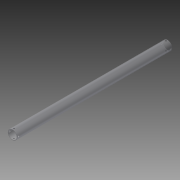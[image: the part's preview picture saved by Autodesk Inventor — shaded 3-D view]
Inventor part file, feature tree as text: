
AUTODESK INVENTOR PART (.ipt)
format: ipt  version: 2014 (Build 180170000, 170)  size: 145,408 bytes
history: native  units: in
note: dims shown in document units (in); Inventor stores cm internally (conversion verified against a paired STEP export)
features: extrude x3, sketch x3, plane x2, projected_geometry x1
ambient origin geometry x8: Origin, YZ Plane, XZ Plane, XY Plane, X Axis, Y Axis, Z Axis, Center Point
bodies: Solid1 (feature_tree)
feature tree (9):
  extrude  "Extrusion1"  Depth=1.125in
  plane  "Work Plane1"
  extrude  "Extrusion2"  Depth=10.5in
  plane  "Work Plane2"
  extrude  "Extrusion3"  Depth=0.2188in
  sketch  "Sketch1"  dims[d0=1.25in d1=1.125in]
  sketch  "Sketch2"  dims[d2=21.0in d3=0.0in d4=10.5in]
  projected_geometry  "Projected Loop1"
  sketch  "Sketch3"  dims[d5=0.19in d6=0.2188in d7=0.625in d8=2.0in d9=0.0in d10=10.5in d11=0.19in d12=0.2188in d13=0.625in d14=2.0in d15=0.0in]
